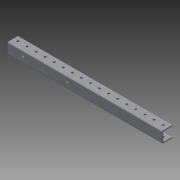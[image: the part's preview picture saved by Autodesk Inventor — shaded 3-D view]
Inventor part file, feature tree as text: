
AUTODESK INVENTOR PART (.ipt)
format: ipt  version: 2015 SP1 (Build 190203100, 203)  size: 164,352 bytes
history: native  units: in
note: dims shown in document units (in); Inventor stores cm internally (conversion verified against a paired STEP export)
features: sketch x5, extrude x3, hole x2, projected_geometry x2, pattern_linear x1, fillet x1
ambient origin geometry x8: Origin, YZ Plane, XZ Plane, XY Plane, X Axis, Y Axis, Z Axis, Center Point
bodies: Solid1 (feature_tree)
feature tree (14):
  extrude  "Extrusion1"  Depth=1.25in
  hole  "Hole1"  [1 undecoded]
  pattern_linear  "Rectangular Pattern1"  Spacing1=16.0in  [1 undecoded]
  hole  "Hole2"  [1 undecoded]
  extrude  "Extrusion3"  Depth=0.125in
  extrude  "Extrusion4"  Depth=1.0in
  fillet  "Fillet1"  Radius=0.625in
  sketch  "Sketch1"  dims[d0=1.125in d2=1.25in]
  sketch  "Sketch2"  dims[d3=90.0deg d4=1.125in]
  projected_geometry  "Projected Loop1"
  sketch  "Sketch4"  dims[d5=90.0deg]
  sketch  "Sketch5"  dims[d6=0.125in]
  sketch  "Sketch6"  dims[d7=0.125in d8=16.0in d9=0.0in d10=0.5in d11=0.5in d12=0.25in d13=0.75in d14=0.375in d15=0.25in d16=0.5635in d17=1.0in d18=0.8108in d19=7.874in d21=1.0in d28=0.625in d30=5.5in d31=0.25in d32=0.75in d33=0.375in d34=0.25in d35=0.5635in d36=1.0in d37=0.8108in d38=1.0in d39=0.0in d40=0.25in d41=0.5in d42=0.5in d43=1.0in d44=0.0in d45=0.6875in d46=0.6875in d47=0.125in]
  projected_geometry  "Projected Loop3"
note: 3 required parameter values undecoded (feature->parameter linkage not recoverable at this tier; creation-order binding heuristic only, values carry confidence <= 0.55)
